# Revit family: Door_Overhead-Coiling-Fire_CHI_7300-Series-Manual
name_source: partatom
category: Doors
units: mm (PartAtom-declared; Revit-internal decimal feet)

## family parameters
Always vertical = Yes
Classification Number = 23.30.10.17.27.11
Cut with Voids When Loaded = No
Host = Wall
Room Calculation Point = No
Shared = No

## types (1)
- As Specified
    Assembly Code = B2030420
    Body Material = Metal - CHI - Silver Powdercoat
    Description = CHI Overhead Door Product as Specified
    Expected Lifespan (Years) = 0
    Fire Rating = As Specified in 08330
    Frame Finish = Metal - CHI - Black Powdercoat
    Function = Interior
    Guide_Btwn Jamb = No
    Guide_E Guide = No
    Guide_Z Guide = Yes
    Height = 9' - 2 1/2"
    Keynote = 08330
    Maintenance Schedule (Months) = 0
    Manufacturer = CHI Overhead Doors
    Max Height = 0' - 0"
    Max Width = 0' - 0"
    Model = as Specified in 08330
    RO Offset = 0' - 0"
    R_Value = 0
    Revision = R1_02-2013
    Rough Height = 9' - 3"
    Rough Width = 9' - 1"
    Slats_Curved = No
    Slats_Flat = Yes
    Sound Transmission Class (STC) = 0
    Thickness = 0' - 0 1/4"
    URL = http://www.chiohd.com
    Voltage_MEP = 0 V
    Wall Closure = By host
    Warranty Duration (Years) = 0
    Width = 9' - 0"

## geometry (parser evidence)
native form markers: Sweep x6
no freeform markers — native parametric forms only
